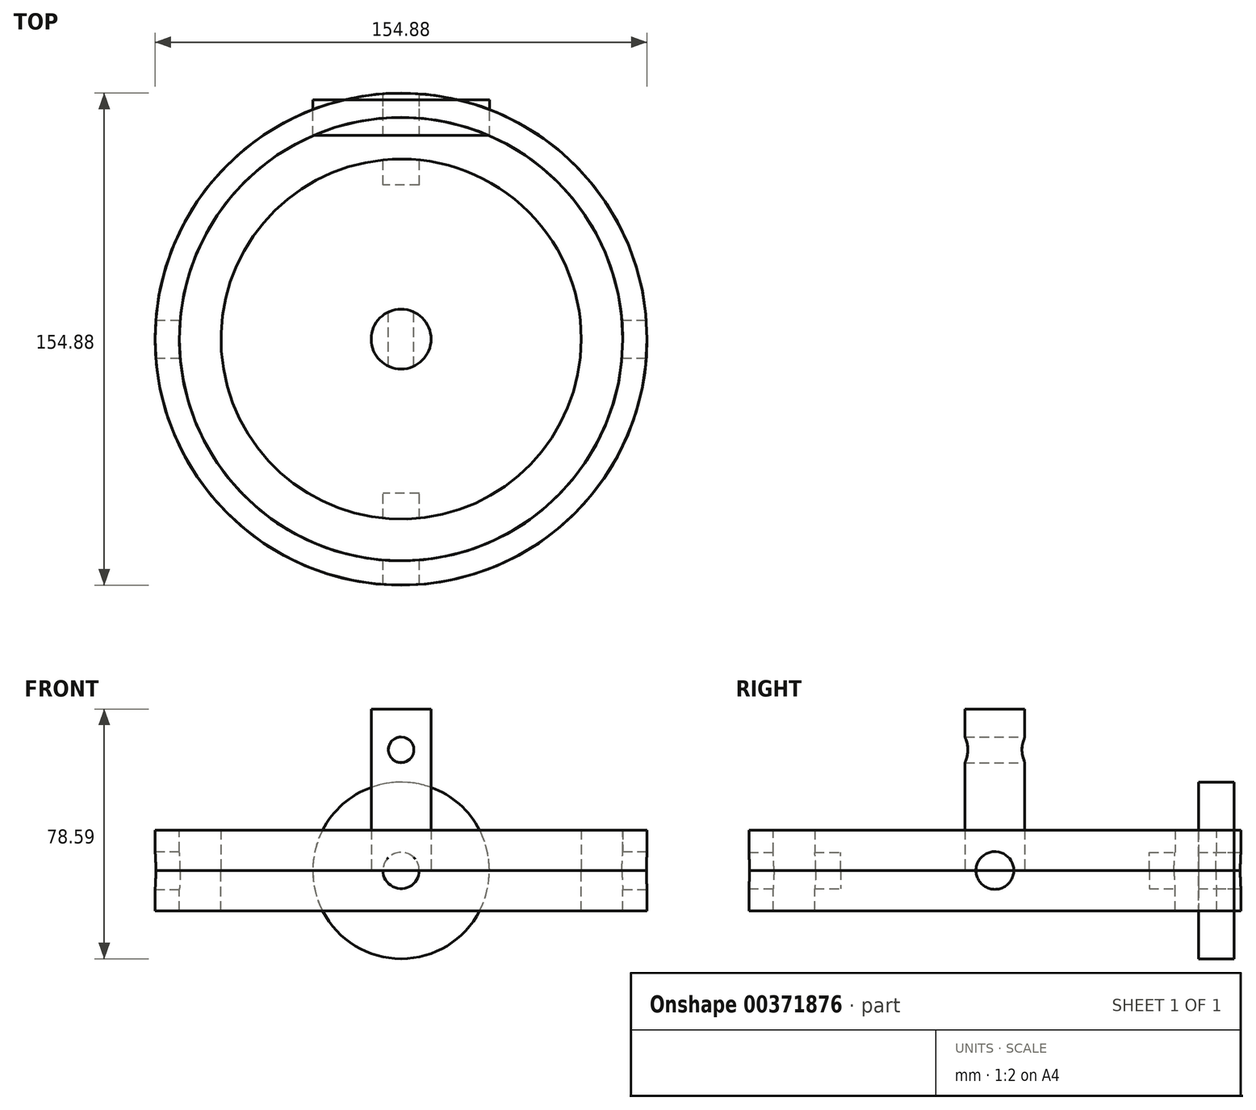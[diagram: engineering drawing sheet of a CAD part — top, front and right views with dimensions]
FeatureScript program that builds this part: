
annotation { "Feature Type Name" : "Feature", "Feature Type Description" : "" }
export const myFeature = defineFeature(function(context is Context, id is Id, definition is map)
    precondition{}
    {
        {
            var Q0;
            Q0=qCreatedBy(makeId("Top.planeOp"),FACE);
            var sketch = newSketch(context, id + "F0", { "sketchPlane" : qUnion([Q0])});
            skCircle(sketch, "E0", {"center": v(0, 0) * mm, "radius": 56.69 * mm});
            skCircle(sketch, "E1", {"center": v(0, 0) * mm, "radius": 69.78 * mm});
            skCircle(sketch, "E2", {"center": v(0, 0) * mm, "radius": 77.44 * mm});
            skSolve(sketch);
        }
        {
            var Q0;
            Q0 = qSketchRegion(id + "F0", true);
            var Q1;
            Q1=makeQuery(id+"F0.imprint","IMPRINT",FACE,{"disambiguationData":[TD([[makeQuery(id+"F0.imprint","IMPRINT",EDGE,{"derivedFrom":sQuery(id+"F0.wireOp",EDGE,"E0")}),1.0]])]});
            extrude(context, id + "F1", {"entities" : qUnion([Q0, Q1]), "depth" : 12.7 * mm, "offsetDistance" : 25.4 * mm});
        }
        {
            var Q0;
            Q0=qCreatedBy(makeId("Top.planeOp"),FACE);
            var sketch = newSketch(context, id + "F2", { "sketchPlane" : qUnion([Q0])});
            skLineSegment(sketch, "E3.bottom", {"start": v(-79.22, 0) * mm, "end": v(-68.64, 0) * mm});
            skLineSegment(sketch, "E3.top", {"start": v(-79.22, 5.94) * mm, "end": v(-68.64, 5.94) * mm});
            skLineSegment(sketch, "E3.left", {"start": v(-79.22, 0) * mm, "end": v(-79.22, 5.94) * mm});
            skLineSegment(sketch, "E3.right", {"start": v(-68.64, 0) * mm, "end": v(-68.64, 5.94) * mm});
            skLineSegment(sketch, "E4.MirrorCS", {"start": v(79.22, 0) * mm, "end": v(68.64, 0) * mm});
            skLineSegment(sketch, "E5.MirrorCS", {"start": v(79.22, 5.94) * mm, "end": v(68.64, 5.94) * mm});
            skLineSegment(sketch, "E6.MirrorCS", {"start": v(79.22, 0) * mm, "end": v(79.22, 5.94) * mm});
            skLineSegment(sketch, "E7.MirrorCS", {"start": v(68.64, 0) * mm, "end": v(68.64, 5.94) * mm});
            skSolve(sketch);
        }
        {
            var Q0;
            Q0=makeQuery(id+"F1.opExtrude","CAP_FACE",FACE,{"disambiguationData":[OSD([sQuery(id+"F0.wireOp",EDGE,"E1"),sQuery(id+"F0.wireOp",EDGE,"E2")])],"isStart":true});
            var Q1;
            Q1=makeQuery(id+"F1.opExtrude","CAP_FACE",FACE,{"disambiguationData":[OSD([sQuery(id+"F0.wireOp",EDGE,"E1"),sQuery(id+"F0.wireOp",EDGE,"E2")])],"isStart":false});
            var Q2;
            Q2=makeQuery(id+"F1.opExtrude","CAP_FACE",FACE,{"disambiguationData":[OSD([sQuery(id+"F0.wireOp",EDGE,"E0")])],"isStart":true});
            extrude(context, id + "F3", {"entities" : qUnion([Q0, Q1, Q2]), "depth" : 12.7 * mm, "offsetDistance" : 25.4 * mm});
        }
        {
            var Q0;
            Q0 = qSketchRegion(id + "F2", true);
            var Q1;
            Q1=sQuery(id+"F2.wireOp",EDGE,"E3.bottom");
            revolve(context, id + "F4", {"operationType" : NewBodyOperationType.REMOVE, "surfaceOperationType" : NewSurfaceOperationType.NEW, "entities" : qUnion([Q0]), "axis" : qUnion([Q1]), "revolveType" : RevolveType.FULL, "oppositeDirection" : true});
        }
        {
            var Q0;
            Q0=qCreatedBy(makeId("Top.planeOp"),FACE);
            var sketch = newSketch(context, id + "F5", { "sketchPlane" : qUnion([Q0])});
            skLineSegment(sketch, "E8.MirrorCS", {"start": v(27.8, 64.08) * mm, "end": v(27.8, 75.26) * mm});
            skLineSegment(sketch, "E9", {"start": v(0, 75.26) * mm, "end": v(0, 64.08) * mm});
            skLineSegment(sketch, "E10", {"start": v(0, 75.26) * mm, "end": v(27.8, 75.26) * mm});
            skLineSegment(sketch, "E11", {"start": v(0, 64.08) * mm, "end": v(27.8, 64.08) * mm});
            skSolve(sketch);
        }
        {
            var Q0;
            Q0 = qSketchRegion(id + "F5", true);
            var Q1;
            Q1=sQuery(id+"F5.wireOp",EDGE,"E9");
            revolve(context, id + "F6", {"surfaceOperationType" : NewSurfaceOperationType.NEW, "entities" : qUnion([Q0]), "axis" : qUnion([Q1]), "revolveType" : RevolveType.FULL});
        }
        {
            var Q0;
            Q0=qCreatedBy(makeId("Top.planeOp"),FACE);
            var sketch = newSketch(context, id + "F7", { "sketchPlane" : qUnion([Q0])});
            skLineSegment(sketch, "E12.bottom", {"start": v(0, 48.55) * mm, "end": v(5.7, 48.55) * mm});
            skLineSegment(sketch, "E12.top", {"start": v(0, 79.14) * mm, "end": v(5.7, 79.14) * mm});
            skLineSegment(sketch, "E12.left", {"start": v(0, 48.55) * mm, "end": v(0, 79.14) * mm});
            skLineSegment(sketch, "E12.right", {"start": v(5.7, 48.55) * mm, "end": v(5.7, 79.14) * mm});
            skLineSegment(sketch, "E13.MirrorCS", {"start": v(0, -48.55) * mm, "end": v(0, -79.14) * mm});
            skLineSegment(sketch, "E14.MirrorCS", {"start": v(5.7, -48.55) * mm, "end": v(5.7, -79.14) * mm});
            skLineSegment(sketch, "E15.MirrorCS", {"start": v(0, -79.14) * mm, "end": v(5.7, -79.14) * mm});
            skLineSegment(sketch, "E16.MirrorCS", {"start": v(0, -48.55) * mm, "end": v(5.7, -48.55) * mm});
            skSolve(sketch);
        }
        {
            var Q0;
            Q0 = qSketchRegion(id + "F7", true);
            var Q1;
            Q1=sQuery(id+"F7.wireOp",EDGE,"E12.left");
            revolve(context, id + "F8", {"operationType" : NewBodyOperationType.REMOVE, "surfaceOperationType" : NewSurfaceOperationType.NEW, "entities" : qUnion([Q0]), "axis" : qUnion([Q1]), "revolveType" : RevolveType.FULL, "oppositeDirection" : true});
        }
        {
            var Q0;
            Q0=qCreatedBy(makeId("Top.planeOp"),FACE);
            var sketch = newSketch(context, id + "F9", { "sketchPlane" : qUnion([Q0])});
            skCircle(sketch, "E17", {"center": v(0, 0) * mm, "radius": 9.42 * mm});
            skSolve(sketch);
        }
        {
            var Q0;
            Q0 = qSketchRegion(id + "F9", true);
            extrude(context, id + "F10", {"entities" : qUnion([Q0]), "depth" : 50.8 * mm, "offsetDistance" : 25.4 * mm});
        }
        {
            var Q0;
            Q0=qCreatedBy(makeId("Front.planeOp"),FACE);
            var sketch = newSketch(context, id + "F11", { "sketchPlane" : qUnion([Q0])});
            skCircle(sketch, "E18", {"center": v(0, 37.98) * mm, "radius": 4.03 * mm});
            skSolve(sketch);
        }
        {
            var Q0;
            Q0 = qSketchRegion(id + "F11", true);
            extrude(context, id + "F12", {"entities" : qUnion([Q0]), "operationType" : NewBodyOperationType.REMOVE, "depth" : 12.7 * mm, "offsetDistance" : 25.4 * mm, "hasSecondDirection" : true, "secondDirectionOppositeDirection" : true, "secondDirectionDepth" : 12.7 * mm});
        }
    });
